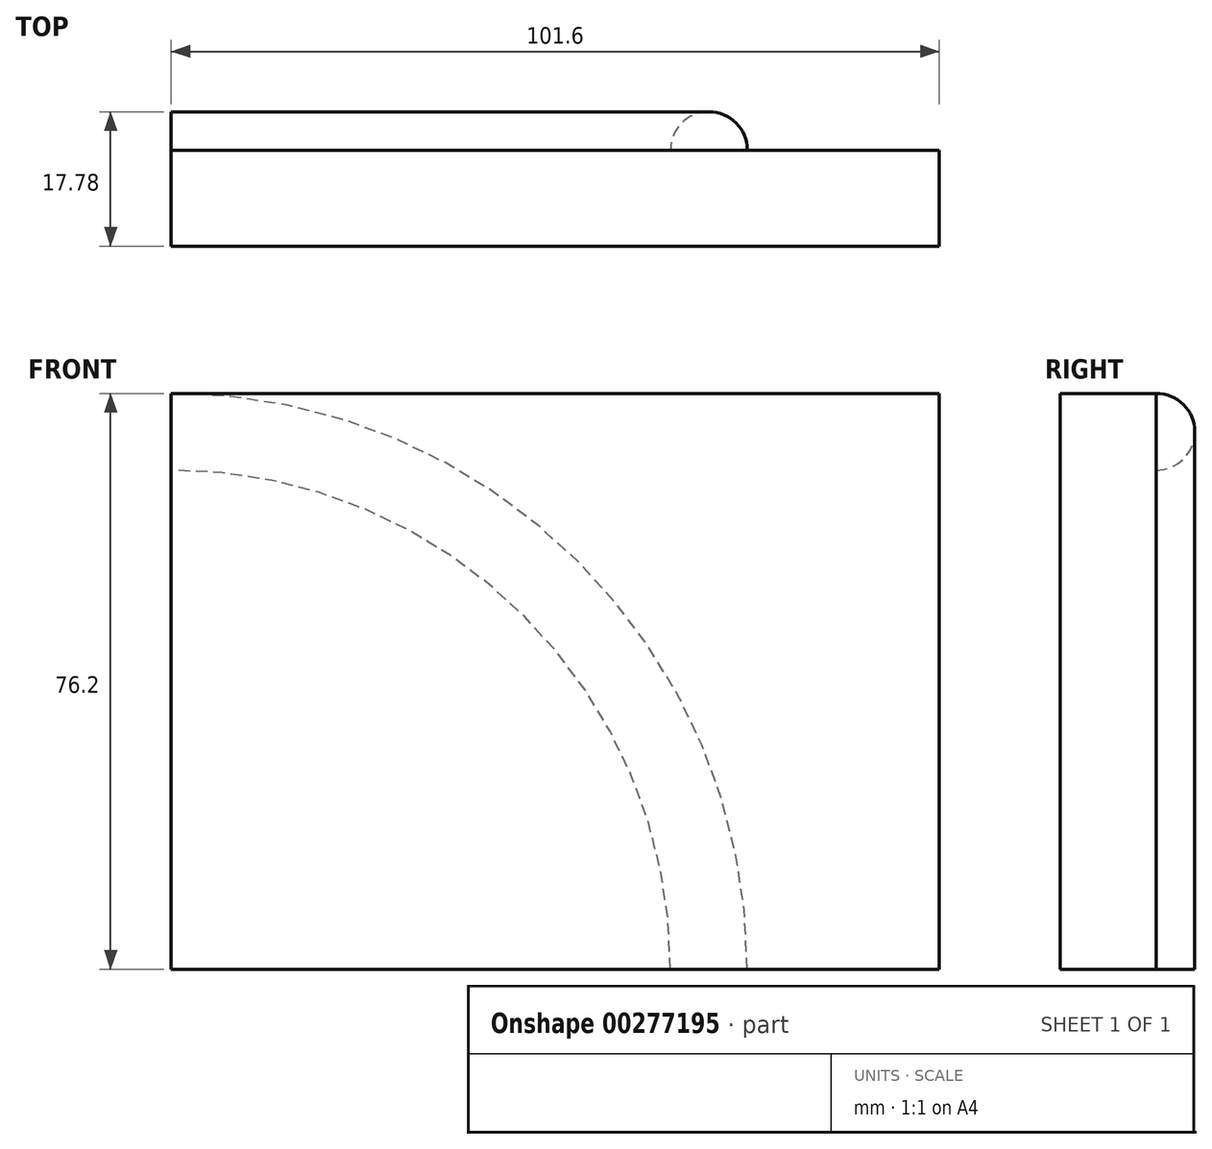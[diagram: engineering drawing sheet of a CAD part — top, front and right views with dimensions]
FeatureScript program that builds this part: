
annotation { "Feature Type Name" : "Feature", "Feature Type Description" : "" }
export const myFeature = defineFeature(function(context is Context, id is Id, definition is map)
    precondition{}
    {
        {
            var Q0;
            Q0=qCreatedBy(makeId("Front.planeOp"),FACE);
            var sketch = newSketch(context, id + "F0", { "sketchPlane" : qUnion([Q0])});
            skLineSegment(sketch, "E0.bottom", {"start": v(0, 0) * mm, "end": v(101.6, 0) * mm});
            skLineSegment(sketch, "E0.top", {"start": v(0, 76.2) * mm, "end": v(101.6, 76.2) * mm});
            skLineSegment(sketch, "E0.left", {"start": v(0, 0) * mm, "end": v(0, 76.2) * mm});
            skLineSegment(sketch, "E0.right", {"start": v(101.6, 0) * mm, "end": v(101.6, 76.2) * mm});
            skSolve(sketch);
        }
        {
            var Q0;
            Q0 = qSketchRegion(id + "F0", true);
            extrude(context, id + "F1", {"entities" : qUnion([Q0]), "depth" : 12.7 * mm});
        }
        {
            var Q0;
            Q0=qCreatedBy(makeId("Front.planeOp"),FACE);
            var sketch = newSketch(context, id + "F2", { "sketchPlane" : qUnion([Q0])});
            skLineSegment(sketch, "E1", {"start": v(0, 0) * mm, "end": v(76.2, 0) * mm});
            skLineSegment(sketch, "E2", {"start": v(0, 0) * mm, "end": v(0, 76.2) * mm});
            skArc(sketch, "E3", {"start": v(76.2, 0) * mm, "mid": v(53.88, 53.88) * mm, "end": v(0, 76.2) * mm});
            skLineSegment(sketch, "E4", {"start": v(0, 76.2) * mm, "end": v(0, 66.04) * mm});
            skLineSegment(sketch, "E5", {"start": v(76.2, 0) * mm, "end": v(66.04, 0) * mm});
            skArc(sketch, "E6", {"start": v(66.04, 0) * mm, "mid": v(46.7, 46.7) * mm, "end": v(0, 66.04) * mm});
            skSolve(sketch);
        }
        {
            var Q0;
            Q0=qCreatedBy(makeId("Top.planeOp"),FACE);
            var sketch = newSketch(context, id + "F3", { "sketchPlane" : qUnion([Q0])});
            skLineSegment(sketch, "E7", {"start": v(13.26, 0) * mm, "end": v(13.26, 5.08) * mm});
            skSolve(sketch);
        }
        {
            var Q0;
            Q0=makeQuery(id+"F2.imprint","IMPRINT",FACE,{"disambiguationData":[TD([[makeQuery(id+"F2.imprint","IMPRINT",EDGE,{"derivedFrom":sQuery(id+"F2.wireOp",EDGE,"E3")}),1.0]])]});
            var Q1;
            Q1=sQuery(id+"F3.wireOp",EDGE,"E7");
            sweep(context, id + "F4", {"profiles" : qUnion([Q0]), "path" : qUnion([Q1])});
        }
        {
            var Q0;
            Q0=makeQuery(id+"F4.opSweep","CAP_EDGE",EDGE,{"disambiguationData":[OSD([sQuery(id+"F2.wireOp",EDGE,"E6"),sQuery(id+"F3.wireOp",VERTEX,"E7.end")])],"isStart":false});
            var Q1;
            Q1=makeQuery(id+"F4.opSweep","CAP_EDGE",EDGE,{"disambiguationData":[OSD([sQuery(id+"F2.wireOp",EDGE,"E3"),sQuery(id+"F3.wireOp",VERTEX,"E7.end")])],"isStart":false});
            fillet(context, id + "F5", {"entities" : qUnion([Q0, Q1]), "radius" : 5.08 * mm, "tangentPropagation" : true, "allowEdgeOverflow" : false});
        }
    });
